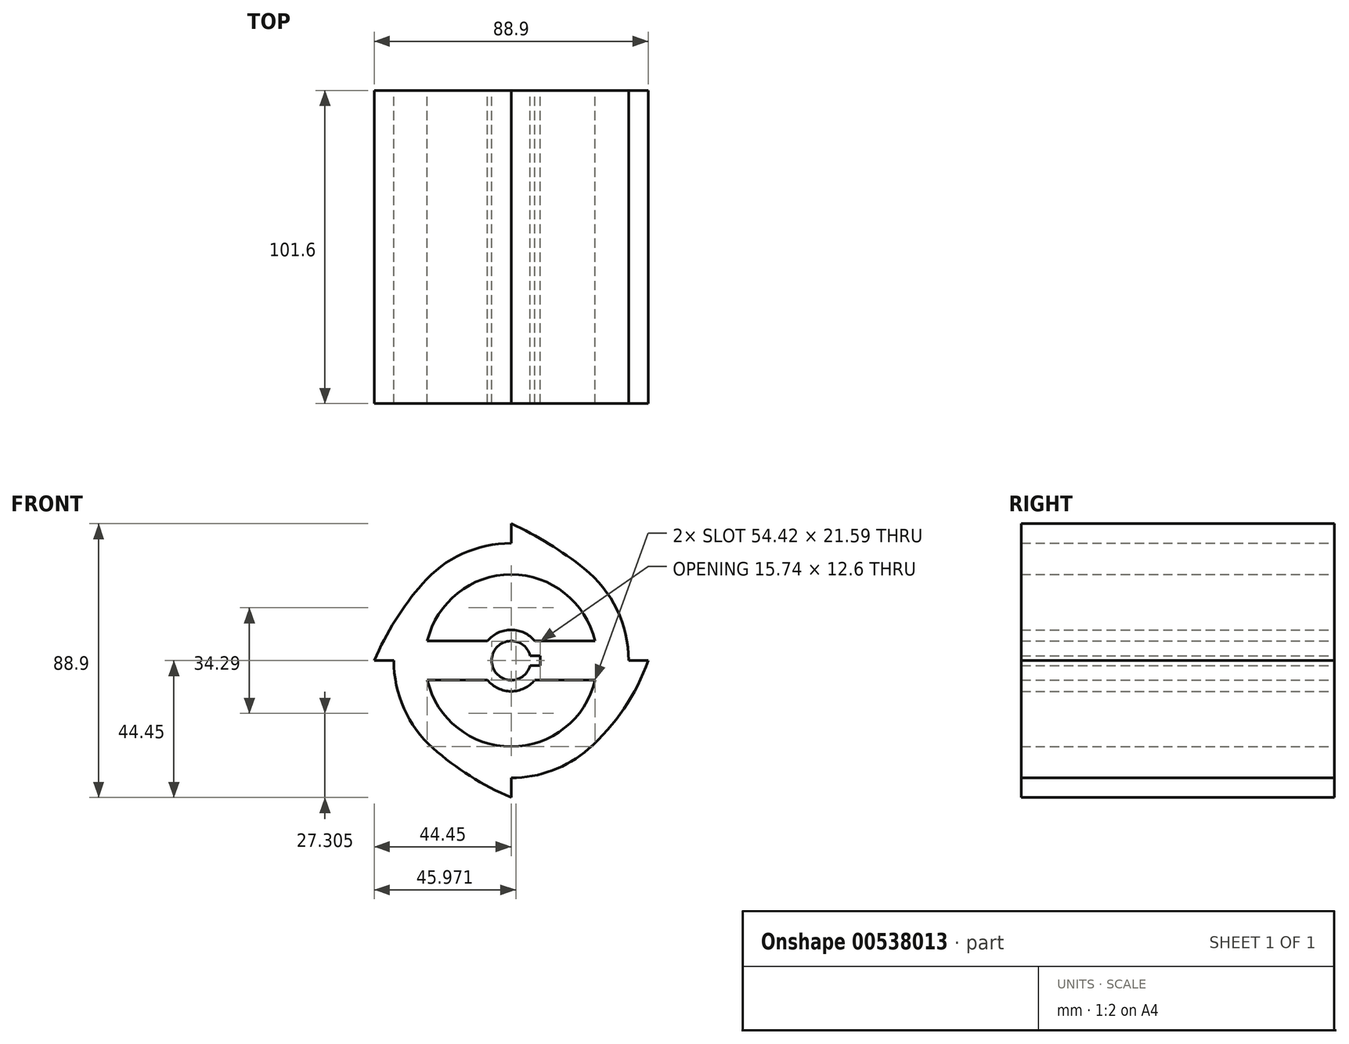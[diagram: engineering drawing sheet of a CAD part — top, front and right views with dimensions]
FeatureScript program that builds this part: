
annotation { "Feature Type Name" : "Feature", "Feature Type Description" : "" }
export const myFeature = defineFeature(function(context is Context, id is Id, definition is map)
    precondition{}
    {
        {
            var Q0;
            Q0=qCreatedBy(makeId("Front.planeOp"),FACE);
            var sketch = newSketch(context, id + "F0", { "sketchPlane" : qUnion([Q0])});
            skCircle(sketch, "E0", {"center": v(0, 0) * mm, "radius": 38.1 * mm});
            skLineSegment(sketch, "E1", {"start": v(-44.45, 0) * mm, "end": v(44.45, 0) * mm});
            skArc(sketch, "E2", {"start": v(23.7, 29.83) * mm, "mid": v(12.29, 37.84) * mm, "end": v(0, 44.45) * mm});
            skArc(sketch, "E3", {"start": v(-28.78, 24.96) * mm, "mid": v(-37.58, 13.09) * mm, "end": v(-44.45, 0) * mm});
            skArc(sketch, "E4", {"start": v(-25.36, -28.44) * mm, "mid": v(-13.34, -37.5) * mm, "end": v(0, -44.45) * mm});
            skArc(sketch, "E5", {"start": v(25.05, -28.7) * mm, "mid": v(36.62, -15.62) * mm, "end": v(44.45, 0) * mm});
            skArc(sketch, "E6", {"start": v(27.2, 6.35) * mm, "mid": v(0, 27.94) * mm, "end": v(-27.2, 6.35) * mm});
            skArc(sketch, "E7", {"start": v(-27.2, -6.35) * mm, "mid": v(0, -27.94) * mm, "end": v(27.2, -6.35) * mm});
            skCircle(sketch, "E8", {"center": v(0, 0) * mm, "radius": 6.35 * mm});
            skLineSegment(sketch, "E9.bottom", {"start": v(-9.4, 1.59) * mm, "end": v(9.4, 1.59) * mm});
            skLineSegment(sketch, "E9.top", {"start": v(-9.4, -1.59) * mm, "end": v(9.4, -1.59) * mm});
            skLineSegment(sketch, "E9.left", {"start": v(-9.4, 1.59) * mm, "end": v(-9.4, -1.59) * mm});
            skLineSegment(sketch, "E9.right", {"start": v(9.4, 1.59) * mm, "end": v(9.4, -1.59) * mm});
            skLineSegment(sketch, "E10", {"start": v(-27.2, -6.35) * mm, "end": v(-7.7, -6.35) * mm});
            skLineSegment(sketch, "E11", {"start": v(-27.2, 6.35) * mm, "end": v(-7.7, 6.35) * mm});
            skLineSegment(sketch, "E12", {"start": v(27.2, -6.35) * mm, "end": v(7.7, -6.35) * mm});
            skLineSegment(sketch, "E13", {"start": v(27.2, 6.35) * mm, "end": v(7.7, 6.35) * mm});
            skCircle(sketch, "E14", {"center": v(0, 0) * mm, "radius": 9.97 * mm});
            skLineSegment(sketch, "E15", {"start": v(0, -44.45) * mm, "end": v(0, -38.1) * mm});
            skLineSegment(sketch, "E16", {"start": v(0, 44.45) * mm, "end": v(0, 38.1) * mm});
            skSolve(sketch);
        }
        {
            var Q0;
            Q0=qSketchRegion(id+"F0",true);
            var Q1;
            {var subQ5=sQuery(id+"F0.wireOp",EDGE,"E14");var subQ6=sQuery(id+"F0.wireOp",EDGE,"E1");var subQ7=makeQuery(id+"F0.imprint","INTERSECT",VERTEX,{"disambiguationData":[OD(0.0)],"derivedFrom":[subQ6,subQ5]});Q1=makeQuery(id+"F0.imprint","IMPRINT",FACE,{"disambiguationData":[TD([[makeQuery(id+"F0.imprint","IMPRINT",EDGE,{"disambiguationData":[TD([[subQ7,-1.0]])],"derivedFrom":subQ6}),-1.0]])]});}
            var Q2;
            {var subQ6=sQuery(id+"F0.wireOp",EDGE,"E1");var subQ10=sQuery(id+"F0.wireOp",EDGE,"E14");var subQ12=makeQuery(id+"F0.imprint","INTERSECT",VERTEX,{"disambiguationData":[OD(0.0)],"derivedFrom":[subQ6,subQ10]});Q2=makeQuery(id+"F0.imprint","IMPRINT",FACE,{"disambiguationData":[TD([[makeQuery(id+"F0.imprint","IMPRINT",EDGE,{"disambiguationData":[TD([[subQ12,-1.0]])],"derivedFrom":subQ6}),1.0]])]});}
            var Q3;
            {var subQ0=sQuery(id+"F0.wireOp",EDGE,"E9.left");var subQ1=sQuery(id+"F0.wireOp",EDGE,"E1");var subQ2=makeQuery(id+"F0.imprint","INTERSECT",VERTEX,{"derivedFrom":[subQ1,subQ0]});Q3=makeQuery(id+"F0.imprint","IMPRINT",FACE,{"disambiguationData":[TD([[makeQuery(id+"F0.imprint","IMPRINT",EDGE,{"disambiguationData":[TD([[subQ2,-1.0]])],"derivedFrom":subQ1}),1.0]])]});}
            var Q4;
            {var subQ0=sQuery(id+"F0.wireOp",EDGE,"E9.left");var subQ1=sQuery(id+"F0.wireOp",EDGE,"E1");var subQ2=makeQuery(id+"F0.imprint","INTERSECT",VERTEX,{"derivedFrom":[subQ1,subQ0]});Q4=makeQuery(id+"F0.imprint","IMPRINT",FACE,{"disambiguationData":[TD([[makeQuery(id+"F0.imprint","IMPRINT",EDGE,{"disambiguationData":[TD([[subQ2,-1.0]])],"derivedFrom":subQ1}),-1.0]])]});}
            extrude(context, id + "F1", {"entities" : qUnion([Q0, Q1, Q2, Q3, Q4]), "depth" : 101.6 * mm, "offsetDistance" : 25.4 * mm});
        }
    });
